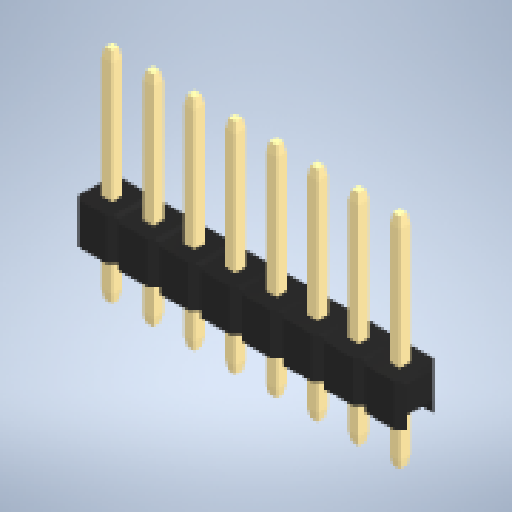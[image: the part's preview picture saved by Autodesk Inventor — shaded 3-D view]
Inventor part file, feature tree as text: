
AUTODESK INVENTOR PART (.ipt)
format: ipt  version: 2023.1 (Build 271208000, 208)  size: 331,776 bytes
history: native  units: in
note: dims shown in document units (in); Inventor stores cm internally (conversion verified against a paired STEP export)
features: other x7, chamfer x1, boolean_combine x1
ambient origin geometry x8: Origin, YZ Plane, XZ Plane, XY Plane, X Axis, Y Axis, Z Axis, Center Point
bodies: Solid1 (feature_tree), Solid2 (feature_tree), Solid3 (feature_tree), Solid4 (feature_tree), Solid5 (feature_tree), Solid6 (feature_tree), Solid7 (feature_tree), Solid8 (feature_tree), Solid9 (feature_tree)
feature tree (9):
  chamfer  "Chamfer3"  [1 undecoded]
  other  "LPattern1[1]"
  other  "LPattern1[2]"
  other  "LPattern1[3]"
  other  "LPattern1[4]"
  other  "LPattern1[5]"
  other  "LPattern1[6]"
  other  "LPattern1[7]"
  boolean_combine  "Combine1"
note: 1 required parameter value undecoded (feature->parameter linkage not recoverable at this tier; creation-order binding heuristic only, values carry confidence <= 0.55)
